# Revit family: Zero Zone - RVLC30
name_source: partatom
category: Specialty Equipment
revit_build: Autodesk Revit 2014 (Build: 20130308_1515(x64)
units: mm (PartAtom-declared; Revit-internal decimal feet)

## types (4) — shared parameters
Base Height = 3 1/2"
Comments = See Zero Zone Sales Spec Sheet
Description = Case, Frozen Food, Ice Cream
Elec Anti-Sweat Type = CoolView
Elec Anti-Sweat Voltage = 115V-1-60
Elec Conn Offset = 27 21/32"
Elec Defrost Type = Electric
Elec Defrost Voltage = 208V-1-60
Elec Fan Type = SSC
Elec Fan Voltage = 115V-1-60
Elec Light Type = LED Zero Zone Chillbrite 4
Elec Light Voltage = 120V-1-60
Height with Elec Box = 83 1/2"
Manufacturer = Zero Zone
Plumbing = 1” PVC Drain
URL = www.zero-zone.com
Width = 39 1/4"
zero-valued in all types: Cost

## per-type parameters (varying)
| type | 2RVLC30 | 3RVLC30 | 4RVLC30 | 5RVLC30 | Description Legend | Doors | Drain Offset | Elec Anti-Sweat Amps | Elec Anti-Sweat Watts | Elec Defrost Amps | Elec Defrost Watts | Elec Fan Amps | Elec Fan Watts | Elec Light Amps | Elec Light Watts | Length | Model | Refr Case BTU FF | Refr Case BTU IC |
| Zero Zone - 4RVLC30 | No | No | Yes | No | 4 Door Freezer, 30 x 74 Doors, Cantilever | 4 | 61 1/2" | 4.02 | 462 | 16.00 | 3,328 | 1.20 | 96 | 0.63 | 77 | 123" | 4RVLC30 | 4,225 | 4,565 |
| Zero Zone - 5RVLC30 | No | No | No | Yes | 5 Door Freezer, 30 x 74 Doors, Cantilever | 5 | 76 3/4" | 5.00 | 575 | 20.00 | 4,160 | 1.50 | 120 | 0.79 | 96 | 153 3/8" | 5RVLC30 | 5,235 | 5,655 |
| Zero Zone - 2RVLC30 | Yes | No | No | No | 2 Door Freezer, 30 x 74 Doors, Cantilever | 2 | 31 1/8" | 2.05 | 236 | 8.00 | 1,664 | 0.60 | 48 | 0.32 | 39 | 62 1/8" | 2RVLC30 | 2,140 | 2,390 |
| Zero Zone - 3RVLC30 | No | Yes | No | No | 3 Door Freezer, 30 x 74 Doors, Cantilever | 3 | 46 1/4" | 3.03 | 349 | 12.00 | 2,496 | 0.90 | 72 | 0.48 | 58 | 92 1/2" | 3RVLC30 | 3,220 | 3,480 |

## geometry (parser evidence)
native form markers: Sweep x3
no freeform markers — native parametric forms only
